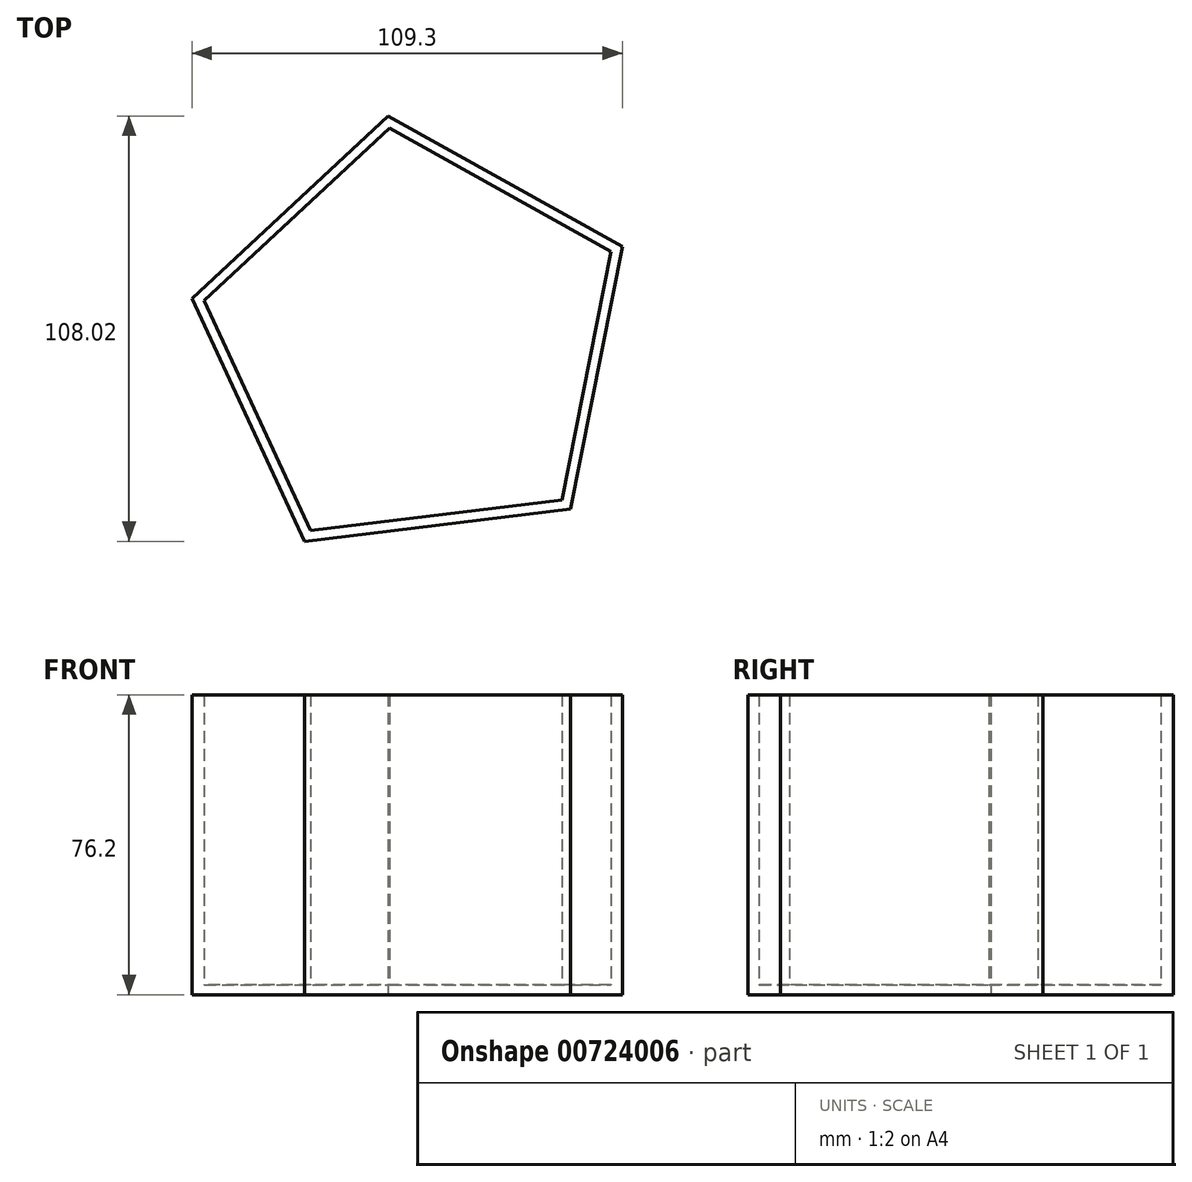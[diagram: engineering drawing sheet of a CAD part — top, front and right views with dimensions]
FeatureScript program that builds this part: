
annotation { "Feature Type Name" : "Feature", "Feature Type Description" : "" }
export const myFeature = defineFeature(function(context is Context, id is Id, definition is map)
    precondition{}
    {
        {
            var Q0;
            Q0=qCreatedBy(makeId("Top.planeOp"),FACE);
            var sketch = newSketch(context, id + "F0", { "sketchPlane" : qUnion([Q0])});
            skCircle(sketch, "E0.cCircle", {"center": v(-38.35, -22.58) * mm, "radius": 46.83 * mm, "construction": true});
            skLineSegment(sketch, "E0.0", {"start": v(-45.3, 34.88) * mm, "end": v(14.15, 1.78) * mm});
            skLineSegment(sketch, "E0.1", {"start": v(14.15, 1.78) * mm, "end": v(1.03, -64.99) * mm});
            skLineSegment(sketch, "E0.2", {"start": v(1.03, -64.99) * mm, "end": v(-66.52, -73.14) * mm});
            skLineSegment(sketch, "E0.3", {"start": v(-66.52, -73.14) * mm, "end": v(-95.15, -11.42) * mm});
            skLineSegment(sketch, "E0.4", {"start": v(-95.15, -11.42) * mm, "end": v(-45.3, 34.88) * mm});
            skPoint(sketch, "E0.0.midPoint", {"position": v(-15.57, 18.33) * mm});
            skSolve(sketch);
        }
        {
            var Q0;
            Q0=makeQuery(id+"F0.imprint","IMPRINT",FACE,{"disambiguationData":[TD([[makeQuery(id+"F0.imprint","IMPRINT",EDGE,{"derivedFrom":sQuery(id+"F0.wireOp",EDGE,"E0.0")}),-1.0]])]});
            extrude(context, id + "F1", {"entities" : qUnion([Q0]), "depth" : 76.2 * mm, "offsetDistance" : 25.4 * mm});
        }
        {
            var Q0;
            Q0=makeQuery(id+"F1.opExtrude","CAP_FACE",FACE,{"disambiguationData":[OSD([sQuery(id+"F0.wireOp",EDGE,"E0.0"),sQuery(id+"F0.wireOp",EDGE,"E0.1"),sQuery(id+"F0.wireOp",EDGE,"E0.2"),sQuery(id+"F0.wireOp",EDGE,"E0.3"),sQuery(id+"F0.wireOp",EDGE,"E0.4")])],"isStart":false});
            shell(context, id + "F2", {"entities" : qUnion([Q0]), "thickness" : 2.54 * mm});
        }
    });
